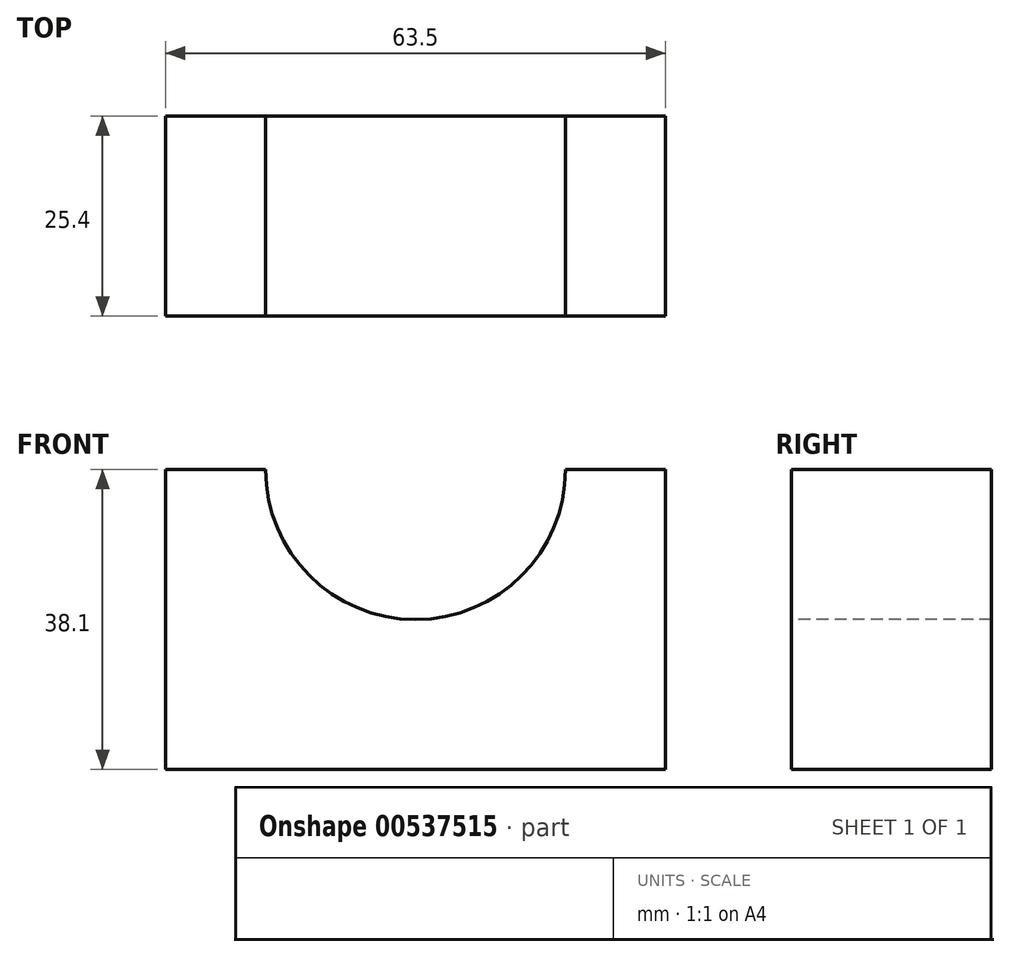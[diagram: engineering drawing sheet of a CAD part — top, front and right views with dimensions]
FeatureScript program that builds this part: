
annotation { "Feature Type Name" : "Feature", "Feature Type Description" : "" }
export const myFeature = defineFeature(function(context is Context, id is Id, definition is map)
    precondition{}
    {
        {
            var Q0;
            Q0=qCreatedBy(makeId("Front.planeOp"),FACE);
            var sketch = newSketch(context, id + "F0", { "sketchPlane" : qUnion([Q0])});
            skLineSegment(sketch, "E0", {"start": v(0, 0) * mm, "end": v(63.5, 0) * mm});
            skLineSegment(sketch, "E1", {"start": v(63.5, 0) * mm, "end": v(63.5, 38.1) * mm});
            skLineSegment(sketch, "E2", {"start": v(63.5, 38.1) * mm, "end": v(0, 38.1) * mm});
            skLineSegment(sketch, "E3", {"start": v(0, 38.1) * mm, "end": v(0, 0) * mm});
            skSolve(sketch);
        }
        {
            var Q0;
            Q0 = qSketchRegion(id + "F0", true);
            extrude(context, id + "F1", {"entities" : qUnion([Q0]), "depth" : 25.4 * mm, "offsetDistance" : 25.4 * mm});
        }
        {
            var Q0;
            Q0=makeQuery(id+"F1.opExtrude","CAP_FACE",FACE,{"disambiguationData":[OSD([sQuery(id+"F0.wireOp",EDGE,"E0"),sQuery(id+"F0.wireOp",EDGE,"E1"),sQuery(id+"F0.wireOp",EDGE,"E2"),sQuery(id+"F0.wireOp",EDGE,"E3")])],"isStart":false});
            var sketch = newSketch(context, id + "F2", { "sketchPlane" : qUnion([Q0])});
            skLineSegment(sketch, "E4", {"start": v(0, 38.1) * mm, "end": v(12.7, 38.1) * mm});
            skLineSegment(sketch, "E5", {"start": v(63.5, 38.1) * mm, "end": v(50.8, 38.1) * mm});
            skLineSegment(sketch, "E6", {"start": v(31.75, 38.1) * mm, "end": v(31.75, 19.05) * mm});
            skArc(sketch, "E7", {"start": v(12.7, 38.1) * mm, "mid": v(31.75, 19.05) * mm, "end": v(50.8, 38.1) * mm});
            skSolve(sketch);
        }
        {
            var Q0;
            Q0 = qSketchRegion(id + "F2", true);
            var Q1;
            {var subQ0=sQuery(id+"F2.wireOp",EDGE,"E6");Q1=makeQuery(id+"F2.imprint","IMPRINT",FACE,{"disambiguationData":[TD([[makeQuery(id+"F2.imprint","IMPRINT",EDGE,{"derivedFrom":subQ0}),-1.0]])]});}
            var Q2;
            {var subQ0=sQuery(id+"F2.wireOp",EDGE,"E6");Q2=makeQuery(id+"F2.imprint","IMPRINT",FACE,{"disambiguationData":[TD([[makeQuery(id+"F2.imprint","IMPRINT",EDGE,{"derivedFrom":subQ0}),1.0]])]});}
            extrude(context, id + "F3", {"entities" : qUnion([Q0, Q1, Q2]), "operationType" : NewBodyOperationType.REMOVE, "oppositeDirection" : true, "depth" : 25.4 * mm, "offsetDistance" : 25.4 * mm});
        }
    });
